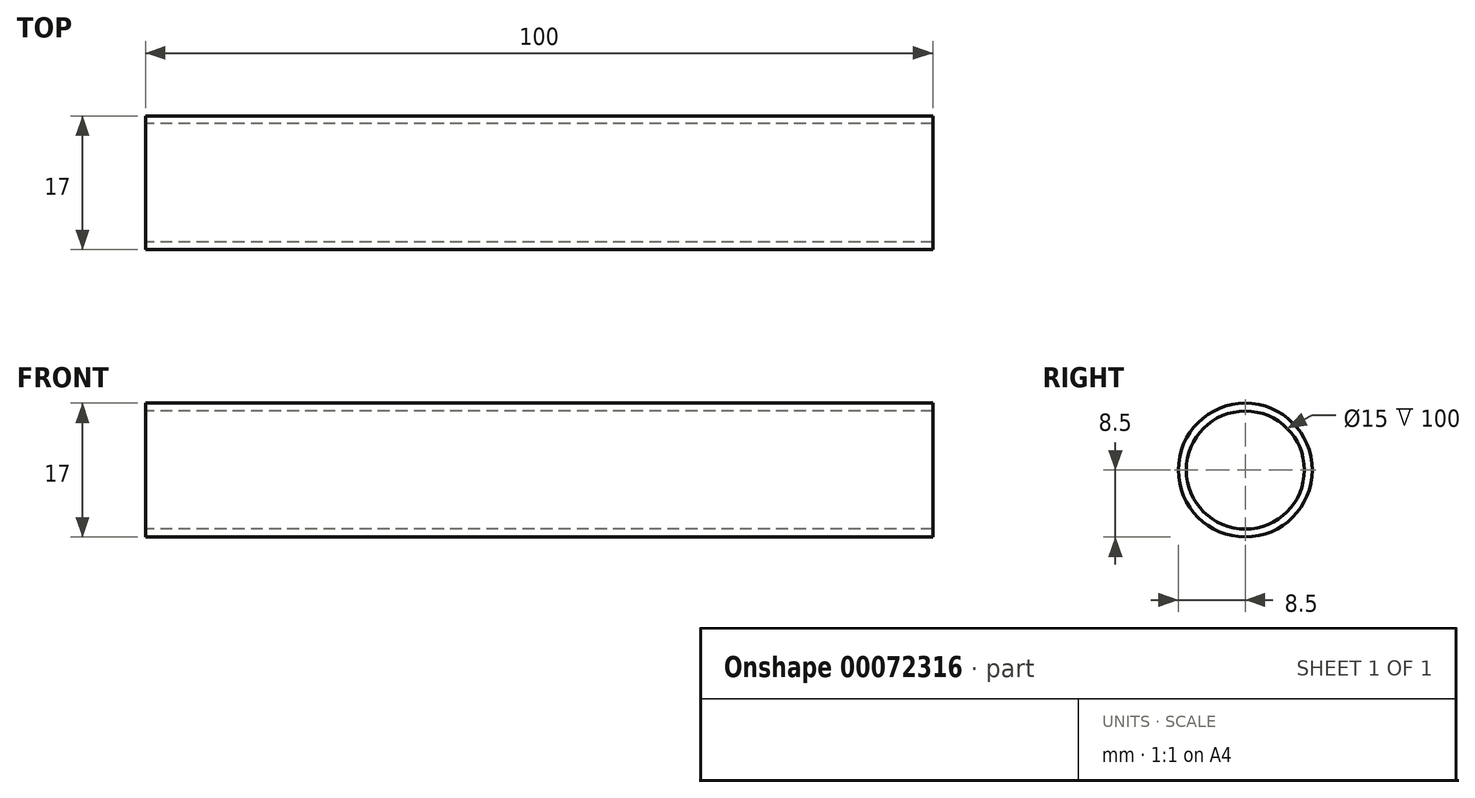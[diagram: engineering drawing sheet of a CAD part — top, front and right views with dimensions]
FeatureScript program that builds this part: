
annotation { "Feature Type Name" : "Feature", "Feature Type Description" : "" }
export const myFeature = defineFeature(function(context is Context, id is Id, definition is map)
    precondition{}
    {
        {
            var Q0;
            Q0=qCreatedBy(makeId("Right.planeOp"),FACE);
            var sketch = newSketch(context, id + "F0", { "sketchPlane" : qUnion([Q0])});
            skCircle(sketch, "E0", {"center": v(0, 0) * mm, "radius": 7.5 * mm});
            skCircle(sketch, "E1", {"center": v(0, 0) * mm, "radius": 8.5 * mm});
            skSolve(sketch);
        }
        {
            var Q0;
            Q0 = qSketchRegion(id + "F0", true);
            extrude(context, id + "F1", {"entities" : qUnion([Q0]), "depth" : 100 * mm});
        }
    });
